# Revit family: AFX-EGRF-
name_source: partatom
category: Lighting Fixtures
units: mm (PartAtom-declared; Revit-internal decimal feet)

## family parameters
Cut with Voids When Loaded = No
Host = Face
Light Source = Yes
Part Type = Normal
Room Calculation Point = No
Round Connector Dimension = Use Diameter
Shared = No

## types (1)
- AFX-EGRF-
    Body Finish = AFX - Metal Powder Coated White
    Color Filter = 16777215
    Default Elevation = 4' - 0"
    Description = Edge Round 12'' LED Flush Mount  -  8 variations
    Dimming Lamp Color Temperature Shift = <None>
    Emit Shape Visible in Rendering = No
    Emit from Circle Diameter = 1' - 0"
    Lamp = LED
    Manufacturer = AFX Inc
    Model = EGRF12
    Photometric Web File = EGRF1216Lxx_IES.IES
    Revit Model Built By = https://servex-us.com
    Screen Finish = AFX - Diffuser Frosted
    Tilt Angle = 90.00°
    Type Comments = EGRF
    URL = https://www.afxinc.com
    Voltage = 120 V
    Wattage Comments = 22 W

## geometry (parser evidence)
native form markers: Sweep x3
no freeform markers — native parametric forms only
